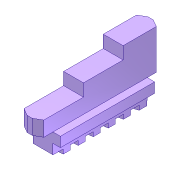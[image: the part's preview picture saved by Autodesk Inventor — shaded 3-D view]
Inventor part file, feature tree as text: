
AUTODESK INVENTOR PART (.ipt)
format: ipt  version: 2016 (Build 200138000, 138)  size: 250,880 bytes
history: native  units: in
note: dims shown in document units (in); Inventor stores cm internally (conversion verified against a paired STEP export)
features: extrude x7, sketch x7, fillet x1, projected_geometry x1
ambient origin geometry x8: Origin, YZ Plane, XZ Plane, XY Plane, X Axis, Y Axis, Z Axis, Center Point
bodies: Solid1 (feature_tree)
feature tree (16):
  extrude  "Extrusion8"  Depth=0.1378in
  extrude  "Extrusion9"  Depth=0.0787in
  extrude  "Extrusion10"  Depth=0.315in
  extrude  "Extrusion11"  TaperAngle=30.0deg  [1 undecoded]
  extrude  "Extrusion13"  Depth=0.7874in TaperAngle=0.0deg
  extrude  "Extrusion14"  Depth=0.1969in TaperAngle=0.0deg
  fillet  "Fillet1"  Radius=0.315in
  extrude  "Extrusion16"  Depth=0.1181in
  sketch  "Sketch10"  dims[d51=0.0787in d52=0.1378in]
  sketch  "Sketch11"  dims[d53=0.0787in d54=0.0787in]
  sketch  "Sketch12"  dims[d55=0.0787in d56=0.315in]
  sketch  "Sketch13"  dims[d57=0.9843in d58=0.0in d59=30.0deg]
  sketch  "Sketch15"  dims[d60=30.0deg d61=0.7874in d62=0.0in]
  sketch  "Sketch16"  dims[d63=0.315in d64=0.1969in d65=0.0in d66=0.315in]
  sketch  "Sketch18"  dims[d67=0.0984in d68=0.0in d72=0.1181in d73=0.1181in d74=0.0787in d75=0.0in d76=0.2874in d79=0.0551in d81=0.0551in d83=0.0551in d85=0.0551in d87=0.0551in d89=0.0551in d90=0.0354in d91=0.0in d92=0.1181in d93=0.1181in d94=0.1181in d95=0.1181in d96=0.1181in d102=0.0008in d103=0.0118in d104=0.0118in d105=0.3937in d106=0.0in]
  projected_geometry  "Projected Loop1"
note: 1 required parameter value undecoded (feature->parameter linkage not recoverable at this tier; creation-order binding heuristic only, values carry confidence <= 0.55)
